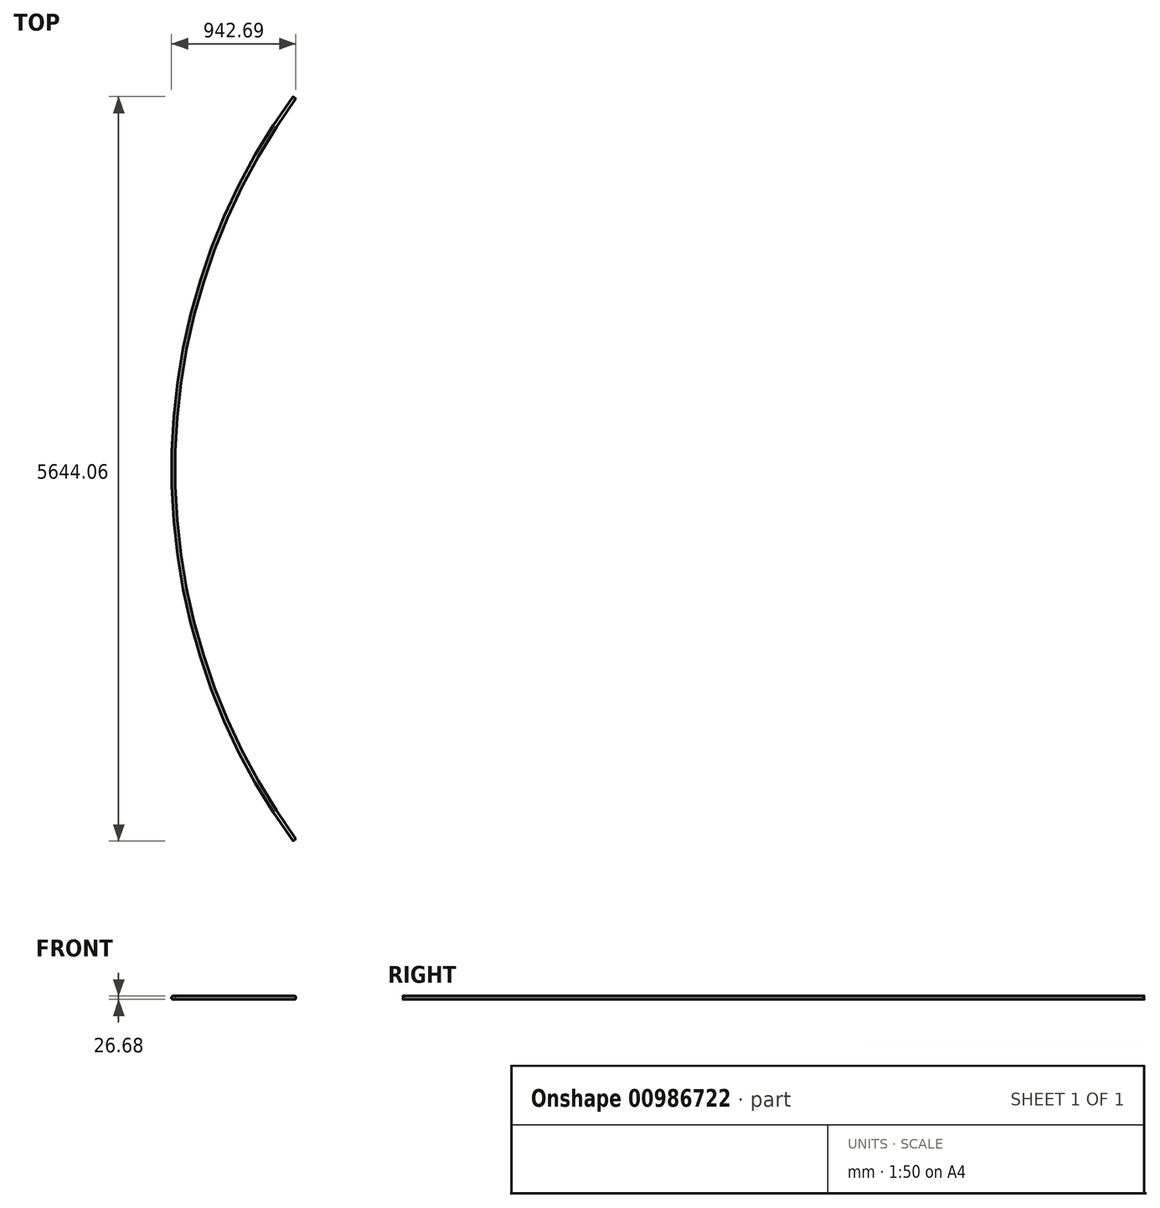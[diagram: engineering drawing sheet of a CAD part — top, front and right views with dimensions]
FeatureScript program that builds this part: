
annotation { "Feature Type Name" : "Feature", "Feature Type Description" : "" }
export const myFeature = defineFeature(function(context is Context, id is Id, definition is map)
    precondition{}
    {
        {
            var Q0;
            Q0=qCreatedBy(makeId("Front.planeOp"),FACE);
            var sketch = newSketch(context, id + "F0", { "sketchPlane" : qUnion([Q0])});
            skLineSegment(sketch, "E0", {"start": v(0, 0) * mm, "end": v(4770, 0) * mm, "construction": true});
            skLineSegment(sketch, "E1", {"start": v(4770, 0) * mm, "end": v(4770, -100) * mm, "construction": true});
            skCircle(sketch, "E2", {"center": v(0, 0) * mm, "radius": 13.34 * mm});
            skCircle(sketch, "E3.0", {"center": v(0, 0) * mm, "radius": 11.23 * mm});
            skSolve(sketch);
        }
        {
            var Q0;
            Q0=qSketchRegion(id+"F0",true);
            var Q1;
            Q1=sQuery(id+"F0.wireOp",EDGE,"E1");
            revolve(context, id + "F1", {"surfaceOperationType" : NewSurfaceOperationType.NEW, "entities" : qUnion([Q0]), "axis" : qUnion([Q1]), "revolveType" : RevolveType.SYMMETRIC, "angle" : 72.31 * degree});
        }
    });
